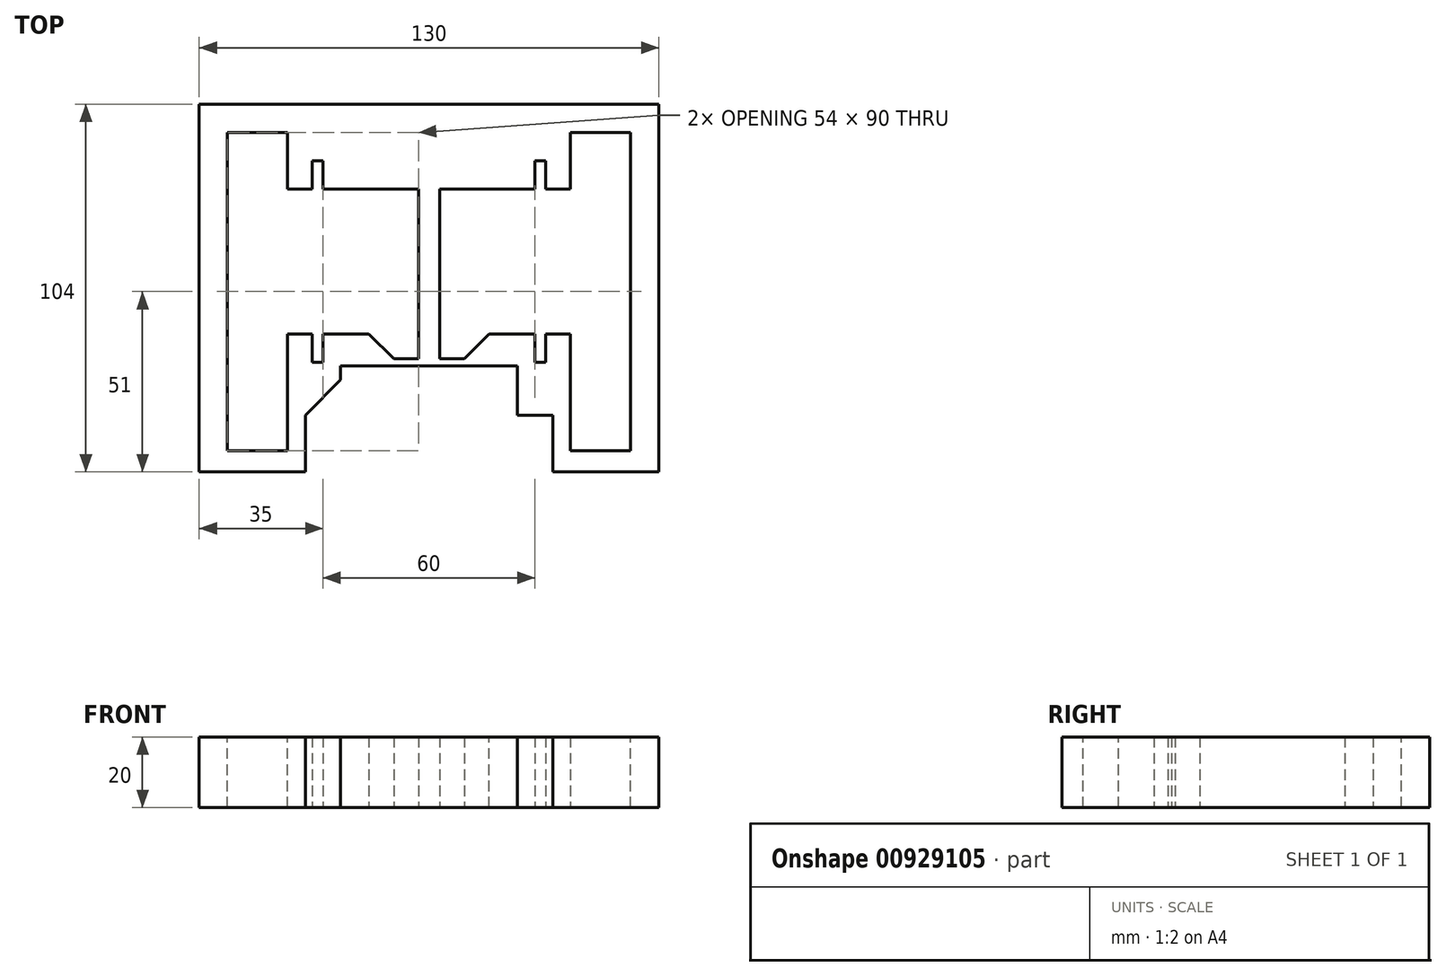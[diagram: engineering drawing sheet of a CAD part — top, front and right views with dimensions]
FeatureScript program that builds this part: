
annotation { "Feature Type Name" : "Feature", "Feature Type Description" : "" }
export const myFeature = defineFeature(function(context is Context, id is Id, definition is map)
    precondition{}
    {
        {
            var Q0;
            Q0=qCreatedBy(makeId("Top.planeOp"),FACE);
            var sketch = newSketch(context, id + "F0", { "sketchPlane" : qUnion([Q0])});
            skLineSegment(sketch, "E0.bottom", {"start": v(0, 0) * mm, "end": v(150, 0) * mm});
            skLineSegment(sketch, "E0.top", {"start": v(0, -90) * mm, "end": v(150, -90) * mm});
            skLineSegment(sketch, "E0.left", {"start": v(0, 0) * mm, "end": v(0, -90) * mm});
            skLineSegment(sketch, "E0.right", {"start": v(150, 0) * mm, "end": v(150, -90) * mm});
            skLineSegment(sketch, "E1", {"start": v(150, 0) * mm, "end": v(0, -90) * mm});
            skLineSegment(sketch, "E2", {"start": v(0, 0) * mm, "end": v(150, -90) * mm});
            skLineSegment(sketch, "E3", {"start": v(75, -45) * mm, "end": v(75, 0) * mm});
            skLineSegment(sketch, "E4", {"start": v(75, 0) * mm, "end": v(75, -90) * mm});
            skLineSegment(sketch, "E5", {"start": v(75, -45) * mm, "end": v(120, -45) * mm});
            skLineSegment(sketch, "E6", {"start": v(75, -45) * mm, "end": v(30, -45) * mm});
            skLineSegment(sketch, "E7.bottom", {"start": v(125, -20) * mm, "end": v(115, -20) * mm});
            skLineSegment(sketch, "E7.top", {"start": v(125, -70) * mm, "end": v(115, -70) * mm});
            skLineSegment(sketch, "E7.left", {"start": v(125, -20) * mm, "end": v(125, -70) * mm});
            skLineSegment(sketch, "E7.right", {"start": v(115, -20) * mm, "end": v(115, -70) * mm});
            skPoint(sketch, "E7.middle", {"position": v(120, -45) * mm});
            skLineSegment(sketch, "E8.bottom", {"start": v(35, -20) * mm, "end": v(25, -20) * mm});
            skLineSegment(sketch, "E8.top", {"start": v(35, -70) * mm, "end": v(25, -70) * mm});
            skLineSegment(sketch, "E8.left", {"start": v(35, -20) * mm, "end": v(35, -70) * mm});
            skLineSegment(sketch, "E8.right", {"start": v(25, -20) * mm, "end": v(25, -70) * mm});
            skPoint(sketch, "E8.middle", {"position": v(30, -45) * mm});
            skLineSegment(sketch, "E9.bottom", {"start": v(35, -45) * mm, "end": v(72, -45) * mm});
            skLineSegment(sketch, "E9.top", {"start": v(35, -14) * mm, "end": v(72, -14) * mm});
            skLineSegment(sketch, "E9.left", {"start": v(35, -45) * mm, "end": v(35, -14) * mm});
            skLineSegment(sketch, "E9.right", {"start": v(72, -45) * mm, "end": v(72, -14) * mm});
            skLineSegment(sketch, "E10.top", {"start": v(35, -55) * mm, "end": v(72, -55) * mm});
            skLineSegment(sketch, "E10.left", {"start": v(35, -45) * mm, "end": v(35, -55) * mm});
            skLineSegment(sketch, "E10.right", {"start": v(72, -45) * mm, "end": v(72, -55) * mm});
            skLineSegment(sketch, "E11.bottom", {"start": v(115, -45) * mm, "end": v(78, -45) * mm});
            skLineSegment(sketch, "E11.top", {"start": v(115, -14) * mm, "end": v(78, -14) * mm});
            skLineSegment(sketch, "E11.left", {"start": v(115, -45) * mm, "end": v(115, -14) * mm});
            skLineSegment(sketch, "E11.right", {"start": v(78, -45) * mm, "end": v(78, -14) * mm});
            skLineSegment(sketch, "E12.top", {"start": v(115, -55) * mm, "end": v(78, -55) * mm});
            skLineSegment(sketch, "E12.left", {"start": v(115, -45) * mm, "end": v(115, -55) * mm});
            skLineSegment(sketch, "E12.right", {"start": v(78, -45) * mm, "end": v(78, -55) * mm});
            skLineSegment(sketch, "E13", {"start": v(72, -14) * mm, "end": v(45, -14) * mm});
            skLineSegment(sketch, "E14.bottom", {"start": v(45, -14) * mm, "end": v(42, -14) * mm});
            skLineSegment(sketch, "E14.top", {"start": v(45, -6) * mm, "end": v(42, -6) * mm});
            skLineSegment(sketch, "E14.left", {"start": v(45, -14) * mm, "end": v(45, -6) * mm});
            skLineSegment(sketch, "E14.right", {"start": v(42, -14) * mm, "end": v(42, -6) * mm});
            skLineSegment(sketch, "E15", {"start": v(72, -45) * mm, "end": v(45, -45) * mm});
            skLineSegment(sketch, "E16", {"start": v(78, -14) * mm, "end": v(105, -14) * mm});
            skLineSegment(sketch, "E17.bottom", {"start": v(105, -14) * mm, "end": v(108, -14) * mm});
            skLineSegment(sketch, "E17.top", {"start": v(105, -6) * mm, "end": v(108, -6) * mm});
            skLineSegment(sketch, "E17.left", {"start": v(105, -14) * mm, "end": v(105, -6) * mm});
            skLineSegment(sketch, "E17.right", {"start": v(108, -14) * mm, "end": v(108, -6) * mm});
            skLineSegment(sketch, "E18", {"start": v(78, -55) * mm, "end": v(105, -55) * mm});
            skLineSegment(sketch, "E19.bottom", {"start": v(105, -55) * mm, "end": v(108, -55) * mm});
            skLineSegment(sketch, "E19.top", {"start": v(105, -63) * mm, "end": v(108, -63) * mm});
            skLineSegment(sketch, "E19.left", {"start": v(105, -55) * mm, "end": v(105, -63) * mm});
            skLineSegment(sketch, "E19.right", {"start": v(108, -55) * mm, "end": v(108, -63) * mm});
            skLineSegment(sketch, "E20.left", {"start": v(78, -55) * mm, "end": v(78, -48) * mm});
            skLineSegment(sketch, "E21.left", {"start": v(72, -55) * mm, "end": v(72, -48) * mm});
            skLineSegment(sketch, "E22.bottom", {"start": v(45, -45) * mm, "end": v(42, -45) * mm});
            skLineSegment(sketch, "E22.top", {"start": v(45, -55) * mm, "end": v(42, -55) * mm});
            skLineSegment(sketch, "E22.left", {"start": v(45, -45) * mm, "end": v(45, -55) * mm});
            skLineSegment(sketch, "E22.right", {"start": v(42, -45) * mm, "end": v(42, -55) * mm});
            skLineSegment(sketch, "E23.top", {"start": v(45, -63) * mm, "end": v(42, -63) * mm});
            skLineSegment(sketch, "E23.left", {"start": v(45, -55) * mm, "end": v(45, -63) * mm});
            skLineSegment(sketch, "E23.right", {"start": v(42, -55) * mm, "end": v(42, -63) * mm});
            skLineSegment(sketch, "E24.bottom", {"start": v(78, -55) * mm, "end": v(85, -55) * mm});
            skLineSegment(sketch, "E24.top", {"start": v(78, -62) * mm, "end": v(85, -62) * mm});
            skLineSegment(sketch, "E24.left", {"start": v(78, -55) * mm, "end": v(78, -62) * mm});
            skLineSegment(sketch, "E24.right", {"start": v(85, -55) * mm, "end": v(85, -62) * mm});
            skLineSegment(sketch, "E25.bottom", {"start": v(72, -55) * mm, "end": v(65, -55) * mm});
            skLineSegment(sketch, "E25.top", {"start": v(72, -62) * mm, "end": v(65, -62) * mm});
            skLineSegment(sketch, "E25.left", {"start": v(72, -55) * mm, "end": v(72, -62) * mm});
            skLineSegment(sketch, "E25.right", {"start": v(65, -55) * mm, "end": v(65, -62) * mm});
            skSolve(sketch);
        }
        {
            var Q0;
            {var subQ1=sQuery(id+"F0.wireOp",EDGE,"E1");var subQ3=sQuery(id+"F0.wireOp",EDGE,"E11.right");var subQ4=makeQuery(id+"F0.imprint","INTERSECT",VERTEX,{"derivedFrom":[subQ1,subQ3]});Q0=makeQuery(id+"F0.imprint","IMPRINT",FACE,{"disambiguationData":[TD([[makeQuery(id+"F0.imprint","IMPRINT",EDGE,{"disambiguationData":[TD([[subQ4,1.0]])],"derivedFrom":subQ3}),1.0]])]});}
            var Q1;
            {var subQ1=sQuery(id+"F0.wireOp",EDGE,"E0.left");Q1=makeQuery(id+"F0.imprint","IMPRINT",FACE,{"disambiguationData":[TD([[makeQuery(id+"F0.imprint","IMPRINT",EDGE,{"derivedFrom":subQ1}),1.0]])]});}
            var Q2;
            {var subQ5=sQuery(id+"F0.wireOp",EDGE,"E0.right");Q2=makeQuery(id+"F0.imprint","IMPRINT",FACE,{"disambiguationData":[TD([[makeQuery(id+"F0.imprint","IMPRINT",EDGE,{"derivedFrom":subQ5}),-1.0]])]});}
            var Q3;
            {var subQ9=sQuery(id+"F0.wireOp",EDGE,"E3");Q3=makeQuery(id+"F0.imprint","IMPRINT",FACE,{"disambiguationData":[TD([[makeQuery(id+"F0.imprint","IMPRINT",EDGE,{"derivedFrom":subQ9}),1.0]])]});}
            var Q4;
            {var subQ5=sQuery(id+"F0.wireOp",EDGE,"E3");Q4=makeQuery(id+"F0.imprint","IMPRINT",FACE,{"disambiguationData":[TD([[makeQuery(id+"F0.imprint","IMPRINT",EDGE,{"derivedFrom":subQ5}),-1.0]])]});}
            var Q5;
            {var subQ1=sQuery(id+"F0.wireOp",EDGE,"E2");var subQ3=sQuery(id+"F0.wireOp",EDGE,"E12.right");var subQ4=makeQuery(id+"F0.imprint","INTERSECT",VERTEX,{"derivedFrom":[subQ1,subQ3]});Q5=makeQuery(id+"F0.imprint","IMPRINT",FACE,{"disambiguationData":[TD([[makeQuery(id+"F0.imprint","IMPRINT",EDGE,{"disambiguationData":[TD([[subQ4,1.0]])],"derivedFrom":subQ3}),-1.0]])]});}
            var Q6;
            {var subQ1=sQuery(id+"F0.wireOp",EDGE,"E2");var subQ3=sQuery(id+"F0.wireOp",EDGE,"E9.right");var subQ4=makeQuery(id+"F0.imprint","INTERSECT",VERTEX,{"derivedFrom":[subQ1,subQ3]});Q6=makeQuery(id+"F0.imprint","IMPRINT",FACE,{"disambiguationData":[TD([[makeQuery(id+"F0.imprint","IMPRINT",EDGE,{"disambiguationData":[TD([[subQ4,1.0]])],"derivedFrom":subQ3}),-1.0]])]});}
            var Q7;
            {var subQ1=sQuery(id+"F0.wireOp",EDGE,"E1");var subQ3=sQuery(id+"F0.wireOp",EDGE,"E10.right");var subQ4=makeQuery(id+"F0.imprint","INTERSECT",VERTEX,{"derivedFrom":[subQ1,subQ3]});Q7=makeQuery(id+"F0.imprint","IMPRINT",FACE,{"disambiguationData":[TD([[makeQuery(id+"F0.imprint","IMPRINT",EDGE,{"disambiguationData":[TD([[subQ4,1.0]])],"derivedFrom":subQ3}),1.0]])]});}
            var Q8;
            {var subQ10=sQuery(id+"F0.wireOp",EDGE,"E21.bottom");Q8=makeQuery(id+"F0.imprint","IMPRINT",FACE,{"disambiguationData":[TD([[makeQuery(id+"F0.imprint","IMPRINT",EDGE,{"derivedFrom":subQ10}),-1.0]])]});}
            var Q9;
            {var subQ5=sQuery(id+"F0.wireOp",EDGE,"E20.bottom");Q9=makeQuery(id+"F0.imprint","IMPRINT",FACE,{"disambiguationData":[TD([[makeQuery(id+"F0.imprint","IMPRINT",EDGE,{"derivedFrom":subQ5}),1.0]])]});}
            var Q10;
            {var subQ11=sQuery(id+"F0.wireOp",EDGE,"E4");Q10=makeQuery(id+"F0.imprint","IMPRINT",FACE,{"disambiguationData":[TD([[makeQuery(id+"F0.imprint","IMPRINT",EDGE,{"derivedFrom":subQ11}),1.0]])]});}
            var Q11;
            {var subQ9=sQuery(id+"F0.wireOp",EDGE,"E4");Q11=makeQuery(id+"F0.imprint","IMPRINT",FACE,{"disambiguationData":[TD([[makeQuery(id+"F0.imprint","IMPRINT",EDGE,{"derivedFrom":subQ9}),-1.0]])]});}
            var Q12;
            {var subQ0=sQuery(id+"F0.wireOp",EDGE,"E23.top");Q12=makeQuery(id+"F0.imprint","IMPRINT",FACE,{"disambiguationData":[TD([[makeQuery(id+"F0.imprint","IMPRINT",EDGE,{"derivedFrom":subQ0}),1.0]])]});}
            var Q13;
            {var subQ0=sQuery(id+"F0.wireOp",EDGE,"E23.left");Q13=makeQuery(id+"F0.imprint","IMPRINT",FACE,{"disambiguationData":[TD([[makeQuery(id+"F0.imprint","IMPRINT",EDGE,{"derivedFrom":subQ0}),1.0]])]});}
            var Q14;
            {var subQ0=sQuery(id+"F0.wireOp",EDGE,"E19.left");Q14=makeQuery(id+"F0.imprint","IMPRINT",FACE,{"disambiguationData":[TD([[makeQuery(id+"F0.imprint","IMPRINT",EDGE,{"derivedFrom":subQ0}),-1.0]])]});}
            var Q15;
            {var subQ0=sQuery(id+"F0.wireOp",EDGE,"E19.top");Q15=makeQuery(id+"F0.imprint","IMPRINT",FACE,{"disambiguationData":[TD([[makeQuery(id+"F0.imprint","IMPRINT",EDGE,{"derivedFrom":subQ0}),-1.0]])]});}
            extrude(context, id + "F1", {"entities" : qUnion([Q0, Q1, Q2, Q3, Q4, Q5, Q6, Q7, Q8, Q9, Q10, Q11, Q12, Q13, Q14, Q15]), "depth" : 20 * mm, "offsetDistance" : 25.4 * mm});
        }
        {
            var Q0;
            Q0=makeQuery(id+"F1.opExtrude","SWEPT_FACE",FACE,{"disambiguationData":[OSD([sQuery(id+"F0.wireOp",EDGE,"E0.top")])]});
            extrude(context, id + "F2", {"entities" : qUnion([Q0]), "operationType" : NewBodyOperationType.REMOVE, "oppositeDirection" : true, "depth" : 12 * mm, "offsetDistance" : 25.4 * mm});
        }
        {
            var Q0;
            Q0=makeQuery(id+"F1.opExtrude","SWEPT_FACE",FACE,{"disambiguationData":[OSD([sQuery(id+"F0.wireOp",EDGE,"E0.right")])]});
            extrude(context, id + "F3", {"entities" : qUnion([Q0]), "operationType" : NewBodyOperationType.REMOVE, "oppositeDirection" : true, "depth" : 10 * mm, "offsetDistance" : 25.4 * mm});
        }
        {
            var Q0;
            Q0=makeQuery(id+"F1.opExtrude","SWEPT_FACE",FACE,{"disambiguationData":[OSD([sQuery(id+"F0.wireOp",EDGE,"E0.left")])]});
            extrude(context, id + "F4", {"entities" : qUnion([Q0]), "operationType" : NewBodyOperationType.REMOVE, "oppositeDirection" : true, "depth" : 10 * mm, "offsetDistance" : 25.4 * mm});
        }
        {
            var Q0;
            Q0=makeQuery(id+"F2.boolean.opBoolean","COPY",FACE,{"derivedFrom":makeQuery(id+"F2.opExtrude","CAP_FACE",FACE,{"disambiguationData":[OSD([sQuery(id+"F0.wireOp",EDGE,"E0.top")])],"isStart":false})});
            var sketch = newSketch(context, id + "F5", { "sketchPlane" : qUnion([Q0])});
            skLineSegment(sketch, "E26", {"start": v(75, 20) * mm, "end": v(75, 0) * mm});
            skLineSegment(sketch, "E27.bottom", {"start": v(100, 20) * mm, "end": v(50, 20) * mm});
            skLineSegment(sketch, "E27.top", {"start": v(100, 0) * mm, "end": v(50, 0) * mm});
            skLineSegment(sketch, "E27.left", {"start": v(100, 20) * mm, "end": v(100, 0) * mm});
            skLineSegment(sketch, "E27.right", {"start": v(50, 20) * mm, "end": v(50, 0) * mm});
            skPoint(sketch, "E27.middle", {"position": v(75, 10) * mm});
            skSolve(sketch);
        }
        {
            var Q0;
            Q0 = qSketchRegion(id + "F5", true);
            extrude(context, id + "F6", {"entities" : qUnion([Q0]), "operationType" : NewBodyOperationType.REMOVE, "oppositeDirection" : true, "depth" : 14 * mm, "offsetDistance" : 25.4 * mm});
        }
        {
            var Q0;
            Q0=makeQuery(id+"F6.boolean.opBoolean","COPY",EDGE,{"derivedFrom":makeQuery(id+"F6.opExtrude","CAP_EDGE",EDGE,{"disambiguationData":[OSD([sQuery(id+"F5.wireOp",EDGE,"E27.left")])],"isStart":true})});
            var Q1;
            Q1=makeQuery(id+"F6.boolean.opBoolean","COPY",EDGE,{"derivedFrom":makeQuery(id+"F6.opExtrude","CAP_EDGE",EDGE,{"disambiguationData":[OSD([sQuery(id+"F5.wireOp",EDGE,"E27.right")])],"isStart":true})});
            chamfer(context, id + "F7", {"entities" : qUnion([Q0, Q1]), "width" : 10 * mm, "tangentPropagation" : true});
        }
        {
            var Q0;
            Q0=makeQuery(id+"F1.opExtrude","SWEPT_EDGE",EDGE,{"disambiguationData":[OSD([sQuery(id+"F0.wireOp",EDGE,"E12.top"),sQuery(id+"F0.wireOp",EDGE,"E24.right")])]});
            var Q1;
            Q1=makeQuery(id+"F1.opExtrude","SWEPT_EDGE",EDGE,{"disambiguationData":[OSD([sQuery(id+"F0.wireOp",EDGE,"E10.top"),sQuery(id+"F0.wireOp",EDGE,"E25.right")])]});
            chamfer(context, id + "F8", {"entities" : qUnion([Q0, Q1]), "width" : 7 * mm, "tangentPropagation" : true});
        }
        {
            var Q0;
            Q0=makeQuery(id+"F1.opExtrude","SWEPT_FACE",FACE,{"disambiguationData":[OSD([sQuery(id+"F0.wireOp",EDGE,"E0.bottom")])]});
            extrude(context, id + "F9", {"entities" : qUnion([Q0]), "operationType" : NewBodyOperationType.ADD, "depth" : 10 * mm, "offsetDistance" : 25.4 * mm});
        }
        {
            var Q0;
            {var subQ0=sQuery(id+"F0.wireOp",EDGE,"E0.bottom");Q0=makeQuery(id+"F9.boolean.opBoolean","MERGE",FACE,{"derivedFrom":[makeQuery(id+"F1.opExtrude","CAP_FACE",FACE,{"disambiguationData":[OSD([subQ0,sQuery(id+"F0.wireOp",EDGE,"E0.top"),sQuery(id+"F0.wireOp",EDGE,"E0.left"),sQuery(id+"F0.wireOp",EDGE,"E0.right"),sQuery(id+"F0.wireOp",EDGE,"E7.bottom"),sQuery(id+"F0.wireOp",EDGE,"E7.top"),sQuery(id+"F0.wireOp",EDGE,"E7.left"),sQuery(id+"F0.wireOp",EDGE,"E7.right"),sQuery(id+"F0.wireOp",EDGE,"E8.bottom"),sQuery(id+"F0.wireOp",EDGE,"E8.top"),sQuery(id+"F0.wireOp",EDGE,"E8.left"),sQuery(id+"F0.wireOp",EDGE,"E8.right"),sQuery(id+"F0.wireOp",EDGE,"E9.top"),sQuery(id+"F0.wireOp",EDGE,"E9.left"),sQuery(id+"F0.wireOp",EDGE,"E9.right"),sQuery(id+"F0.wireOp",EDGE,"E10.top"),sQuery(id+"F0.wireOp",EDGE,"E10.right"),sQuery(id+"F0.wireOp",EDGE,"E11.top"),sQuery(id+"F0.wireOp",EDGE,"E11.left"),sQuery(id+"F0.wireOp",EDGE,"E11.right"),sQuery(id+"F0.wireOp",EDGE,"E12.top"),sQuery(id+"F0.wireOp",EDGE,"E12.right"),sQuery(id+"F0.wireOp",EDGE,"E14.top"),sQuery(id+"F0.wireOp",EDGE,"E14.left"),sQuery(id+"F0.wireOp",EDGE,"E14.right"),sQuery(id+"F0.wireOp",EDGE,"E17.top"),sQuery(id+"F0.wireOp",EDGE,"E17.left"),sQuery(id+"F0.wireOp",EDGE,"E17.right"),sQuery(id+"F0.wireOp",EDGE,"E19.top"),sQuery(id+"F0.wireOp",EDGE,"E19.left"),sQuery(id+"F0.wireOp",EDGE,"E19.right"),sQuery(id+"F0.wireOp",EDGE,"E23.top"),sQuery(id+"F0.wireOp",EDGE,"E23.left"),sQuery(id+"F0.wireOp",EDGE,"E23.right"),sQuery(id+"F0.wireOp",EDGE,"E24.top"),sQuery(id+"F0.wireOp",EDGE,"E24.left"),sQuery(id+"F0.wireOp",EDGE,"E24.right"),sQuery(id+"F0.wireOp",EDGE,"E25.top"),sQuery(id+"F0.wireOp",EDGE,"E25.left"),sQuery(id+"F0.wireOp",EDGE,"E25.right")])],"isStart":false}),makeQuery(id+"F9.opExtrude","SWEPT_FACE",FACE,{"disambiguationData":[OSD([subQ0]),TDD([makeQuery(id+"F1.opExtrude","CAP_EDGE",EDGE,{"disambiguationData":[OSD([subQ0])],"isStart":false})])]})]});}
            var sketch = newSketch(context, id + "F10", { "sketchPlane" : qUnion([Q0])});
            skLineSegment(sketch, "E28.bottom", {"start": v(35, -78) * mm, "end": v(18, -78) * mm});
            skLineSegment(sketch, "E28.top", {"start": v(35, 2) * mm, "end": v(18, 2) * mm});
            skLineSegment(sketch, "E28.left", {"start": v(35, -78) * mm, "end": v(35, 2) * mm});
            skLineSegment(sketch, "E28.right", {"start": v(18, -78) * mm, "end": v(18, 2) * mm});
            skLineSegment(sketch, "E29.bottom", {"start": v(115, -78) * mm, "end": v(132, -78) * mm});
            skLineSegment(sketch, "E29.top", {"start": v(115, 2) * mm, "end": v(132, 2) * mm});
            skLineSegment(sketch, "E29.left", {"start": v(115, -78) * mm, "end": v(115, 2) * mm});
            skLineSegment(sketch, "E29.right", {"start": v(132, -78) * mm, "end": v(132, 2) * mm});
            skSolve(sketch);
        }
        {
            var Q0;
            Q0 = qSketchRegion(id + "F10", true);
            extrude(context, id + "F11", {"entities" : qUnion([Q0]), "operationType" : NewBodyOperationType.REMOVE, "endBound" : BoundingType.THROUGH_ALL, "oppositeDirection" : true, "depth" : 25.4 * mm, "offsetDistance" : 25.4 * mm});
        }
        {
            var Q0;
            {var subQ0=sQuery(id+"F0.wireOp",EDGE,"E0.bottom");Q0=makeQuery(id+"F9.boolean.opBoolean","MERGE",FACE,{"derivedFrom":[makeQuery(id+"F1.opExtrude","CAP_FACE",FACE,{"disambiguationData":[OSD([subQ0,sQuery(id+"F0.wireOp",EDGE,"E0.top"),sQuery(id+"F0.wireOp",EDGE,"E0.left"),sQuery(id+"F0.wireOp",EDGE,"E0.right"),sQuery(id+"F0.wireOp",EDGE,"E7.bottom"),sQuery(id+"F0.wireOp",EDGE,"E7.top"),sQuery(id+"F0.wireOp",EDGE,"E7.left"),sQuery(id+"F0.wireOp",EDGE,"E7.right"),sQuery(id+"F0.wireOp",EDGE,"E8.bottom"),sQuery(id+"F0.wireOp",EDGE,"E8.top"),sQuery(id+"F0.wireOp",EDGE,"E8.left"),sQuery(id+"F0.wireOp",EDGE,"E8.right"),sQuery(id+"F0.wireOp",EDGE,"E9.top"),sQuery(id+"F0.wireOp",EDGE,"E9.left"),sQuery(id+"F0.wireOp",EDGE,"E9.right"),sQuery(id+"F0.wireOp",EDGE,"E10.top"),sQuery(id+"F0.wireOp",EDGE,"E10.right"),sQuery(id+"F0.wireOp",EDGE,"E11.top"),sQuery(id+"F0.wireOp",EDGE,"E11.left"),sQuery(id+"F0.wireOp",EDGE,"E11.right"),sQuery(id+"F0.wireOp",EDGE,"E12.top"),sQuery(id+"F0.wireOp",EDGE,"E12.right"),sQuery(id+"F0.wireOp",EDGE,"E14.top"),sQuery(id+"F0.wireOp",EDGE,"E14.left"),sQuery(id+"F0.wireOp",EDGE,"E14.right"),sQuery(id+"F0.wireOp",EDGE,"E17.top"),sQuery(id+"F0.wireOp",EDGE,"E17.left"),sQuery(id+"F0.wireOp",EDGE,"E17.right"),sQuery(id+"F0.wireOp",EDGE,"E19.top"),sQuery(id+"F0.wireOp",EDGE,"E19.left"),sQuery(id+"F0.wireOp",EDGE,"E19.right"),sQuery(id+"F0.wireOp",EDGE,"E23.top"),sQuery(id+"F0.wireOp",EDGE,"E23.left"),sQuery(id+"F0.wireOp",EDGE,"E23.right"),sQuery(id+"F0.wireOp",EDGE,"E24.top"),sQuery(id+"F0.wireOp",EDGE,"E24.left"),sQuery(id+"F0.wireOp",EDGE,"E24.right"),sQuery(id+"F0.wireOp",EDGE,"E25.top"),sQuery(id+"F0.wireOp",EDGE,"E25.left"),sQuery(id+"F0.wireOp",EDGE,"E25.right")])],"isStart":false}),makeQuery(id+"F9.opExtrude","SWEPT_FACE",FACE,{"disambiguationData":[OSD([subQ0]),TDD([makeQuery(id+"F1.opExtrude","CAP_EDGE",EDGE,{"disambiguationData":[OSD([subQ0])],"isStart":false})])]})]});}
            var sketch = newSketch(context, id + "F12", { "sketchPlane" : qUnion([Q0])});
            skLineSegment(sketch, "E30.bottom", {"start": v(18, 2) * mm, "end": v(35, 2) * mm});
            skLineSegment(sketch, "E30.top", {"start": v(18, -88) * mm, "end": v(35, -88) * mm});
            skLineSegment(sketch, "E30.left", {"start": v(18, 2) * mm, "end": v(18, -88) * mm});
            skLineSegment(sketch, "E30.right", {"start": v(35, 2) * mm, "end": v(35, -88) * mm});
            skLineSegment(sketch, "E31.bottom", {"start": v(132, 2) * mm, "end": v(115, 2) * mm});
            skLineSegment(sketch, "E31.top", {"start": v(132, -88) * mm, "end": v(115, -88) * mm});
            skLineSegment(sketch, "E31.left", {"start": v(132, 2) * mm, "end": v(132, -88) * mm});
            skLineSegment(sketch, "E31.right", {"start": v(115, 2) * mm, "end": v(115, -88) * mm});
            skLineSegment(sketch, "E32.bottom", {"start": v(10, -78) * mm, "end": v(40, -78) * mm});
            skLineSegment(sketch, "E32.top", {"start": v(10, -94) * mm, "end": v(40, -94) * mm});
            skLineSegment(sketch, "E32.left", {"start": v(10, -78) * mm, "end": v(10, -94) * mm});
            skLineSegment(sketch, "E32.right", {"start": v(40, -78) * mm, "end": v(40, -94) * mm});
            skLineSegment(sketch, "E33.bottom", {"start": v(110, -78) * mm, "end": v(140, -78) * mm});
            skLineSegment(sketch, "E33.top", {"start": v(110, -94) * mm, "end": v(140, -94) * mm});
            skLineSegment(sketch, "E33.left", {"start": v(110, -78) * mm, "end": v(110, -94) * mm});
            skLineSegment(sketch, "E33.right", {"start": v(140, -78) * mm, "end": v(140, -94) * mm});
            skSolve(sketch);
        }
        {
            var Q0;
            {var subQ3=sQuery(id+"F12.wireOp",EDGE,"E30.top");Q0=makeQuery(id+"F12.imprint","IMPRINT",FACE,{"disambiguationData":[TD([[makeQuery(id+"F12.imprint","IMPRINT",EDGE,{"derivedFrom":subQ3}),-1.0]])]});}
            var Q1;
            {var subQ8=sQuery(id+"F12.wireOp",EDGE,"E31.top");Q1=makeQuery(id+"F12.imprint","IMPRINT",FACE,{"disambiguationData":[TD([[makeQuery(id+"F12.imprint","IMPRINT",EDGE,{"derivedFrom":subQ8}),1.0]])]});}
            extrude(context, id + "F13", {"entities" : qUnion([Q0, Q1]), "operationType" : NewBodyOperationType.ADD, "oppositeDirection" : true, "depth" : 20 * mm, "offsetDistance" : 25.4 * mm});
        }
    });
